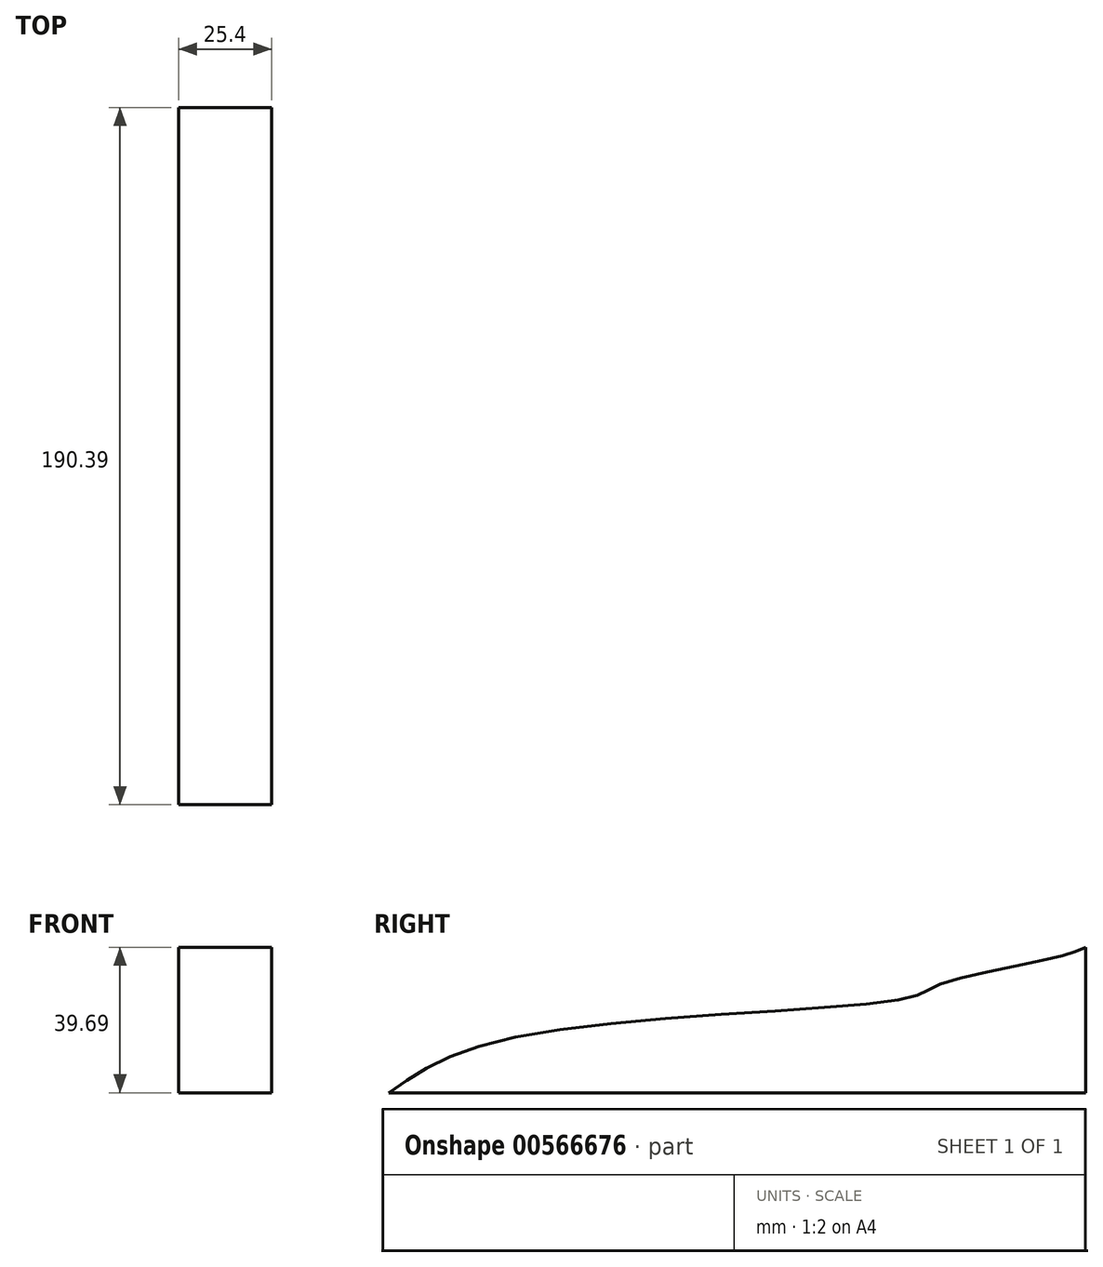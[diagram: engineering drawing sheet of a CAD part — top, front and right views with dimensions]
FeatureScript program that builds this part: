
annotation { "Feature Type Name" : "Feature", "Feature Type Description" : "" }
export const myFeature = defineFeature(function(context is Context, id is Id, definition is map)
    precondition{}
    {
        {
            var Q0;
            Q0=qCreatedBy(makeId("Right.planeOp"),FACE);
            var sketch = newSketch(context, id + "F0", { "sketchPlane" : qUnion([Q0])});
            skLineSegment(sketch, "E0", {"start": v(-94.68, 0) * mm, "end": v(95.7, 0) * mm});
            skLineSegment(sketch, "E1", {"start": v(95.7, 0) * mm, "end": v(95.7, 12.38) * mm});
            skLineSegment(sketch, "E2", {"start": v(95.7, 12.38) * mm, "end": v(95.7, 25.14) * mm});
            skLineSegment(sketch, "E3", {"start": v(95.7, 25.14) * mm, "end": v(95.7, 39.69) * mm});
            skFitSpline(sketch, "E4", {"points": [v(95.7, 39.69) * mm, v(87.03, 36.88) * mm, v(55.64, 29.48) * mm, v(47.47, 25.9) * mm, v(-59.98, 15.19) * mm, v(-94.68, 0) * mm], "startDerivative": vector(-59.24, -24.14) * mm, "endDerivative": vector(-111.21, -78.55) * mm});
            skSolve(sketch);
        }
        {
            var Q0;
            Q0=makeQuery(id+"F0.imprint","IMPRINT",FACE,{"disambiguationData":[TD([[makeQuery(id+"F0.imprint","IMPRINT",EDGE,{"derivedFrom":sQuery(id+"F0.wireOp",EDGE,"E0")}),1.0]])]});
            extrude(context, id + "F1", {"entities" : qUnion([Q0]), "depth" : 25.4 * mm, "offsetDistance" : 25.4 * mm});
        }
    });
